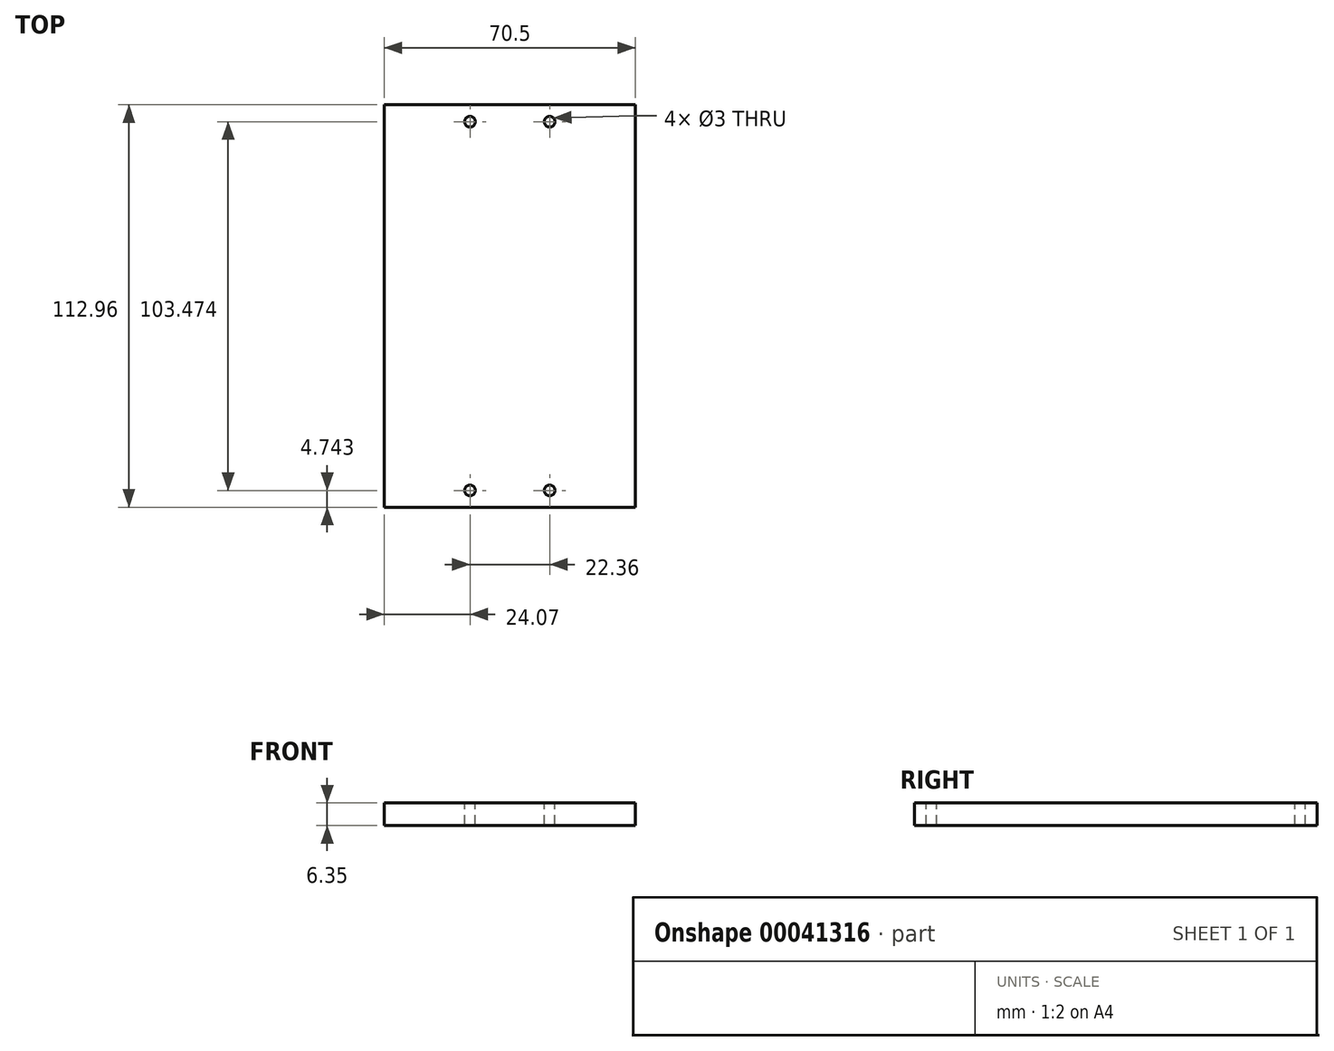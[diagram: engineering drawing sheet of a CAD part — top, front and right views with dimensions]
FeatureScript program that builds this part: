
annotation { "Feature Type Name" : "Feature", "Feature Type Description" : "" }
export const myFeature = defineFeature(function(context is Context, id is Id, definition is map)
    precondition{}
    {
        {
            var Q0;
            Q0=qCreatedBy(makeId("Top.planeOp"),FACE);
            var sketch = newSketch(context, id + "F0", { "sketchPlane" : qUnion([Q0])});
            skLineSegment(sketch, "E0.rect.bottom", {"start": v(35.25, 56.48) * mm, "end": v(-35.25, 56.48) * mm});
            skLineSegment(sketch, "E0.rect.top", {"start": v(35.25, -56.48) * mm, "end": v(-35.25, -56.48) * mm});
            skLineSegment(sketch, "E0.rect.left", {"start": v(35.25, 56.48) * mm, "end": v(35.25, -56.48) * mm});
            skLineSegment(sketch, "E0.rect.right", {"start": v(-35.25, 56.48) * mm, "end": v(-35.25, -56.48) * mm});
            skPoint(sketch, "E0.rect.middle", {"position": v(0, 0) * mm});
            skSolve(sketch);
        }
        {
            var Q0;
            Q0 = qSketchRegion(id + "F0", true);
            extrude(context, id + "F1", {"entities" : qUnion([Q0]), "depth" : 6.35 * mm});
        }
        {
            var Q0;
            Q0=makeQuery(id+"F1.opExtrude","CAP_FACE",FACE,{"disambiguationData":[OSD([sQuery(id+"F0.wireOp",EDGE,"E0.rect.bottom"),sQuery(id+"F0.wireOp",EDGE,"E0.rect.top"),sQuery(id+"F0.wireOp",EDGE,"E0.rect.left"),sQuery(id+"F0.wireOp",EDGE,"E0.rect.right")])],"isStart":false});
            var sketch = newSketch(context, id + "F2", { "sketchPlane" : qUnion([Q0])});
            skLineSegment(sketch, "E1", {"start": v(0, -51.74) * mm, "end": v(0, -56.48) * mm});
            skLineSegment(sketch, "E2", {"start": v(-11.18, -51.74) * mm, "end": v(11.18, -51.74) * mm});
            skCircle(sketch, "E3", {"center": v(-11.18, -51.74) * mm, "radius": 1.5 * mm});
            skCircle(sketch, "E4", {"center": v(11.18, -51.74) * mm, "radius": 1.5 * mm});
            skLineSegment(sketch, "E5.MirrorCS", {"start": v(-11.18, 51.74) * mm, "end": v(11.18, 51.74) * mm});
            skCircle(sketch, "E6.MirrorC", {"center": v(-11.18, 51.74) * mm, "radius": 1.5 * mm});
            skCircle(sketch, "E7.MirrorC", {"center": v(11.18, 51.74) * mm, "radius": 1.5 * mm});
            skSolve(sketch);
        }
        {
            var Q0;
            Q0 = qSketchRegion(id + "F2", true);
            extrude(context, id + "F3", {"entities" : qUnion([Q0]), "operationType" : NewBodyOperationType.REMOVE, "endBound" : BoundingType.UP_TO_NEXT, "oppositeDirection" : true, "depth" : 25.4 * mm});
        }
    });
